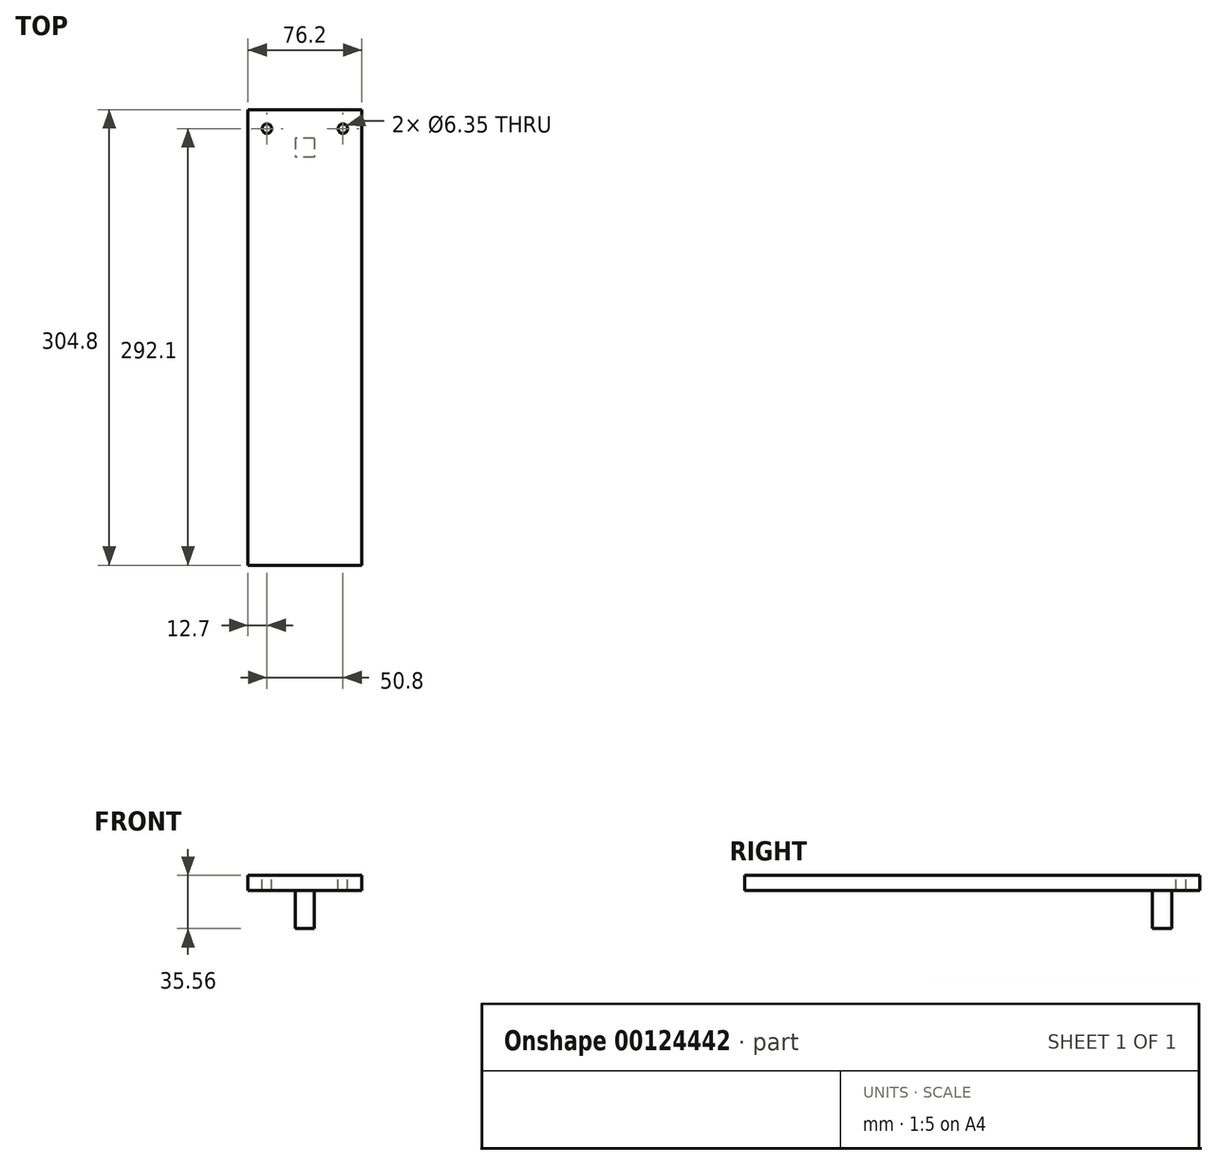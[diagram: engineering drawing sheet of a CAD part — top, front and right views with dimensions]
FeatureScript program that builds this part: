
annotation { "Feature Type Name" : "Feature", "Feature Type Description" : "" }
export const myFeature = defineFeature(function(context is Context, id is Id, definition is map)
    precondition{}
    {
        {
            var Q0;
            Q0=qCreatedBy(makeId("Top.planeOp"),FACE);
            var sketch = newSketch(context, id + "F0", { "sketchPlane" : qUnion([Q0])});
            skPoint(sketch, "E0.middle", {"position": v(0, 0) * mm});
            skLineSegment(sketch, "E1", {"start": v(-38.1, -76.2) * mm, "end": v(-38.1, 152.4) * mm});
            skLineSegment(sketch, "E2", {"start": v(38.1, -76.2) * mm, "end": v(38.1, 152.4) * mm});
            skLineSegment(sketch, "E3", {"start": v(38.1, 152.4) * mm, "end": v(-38.1, 152.4) * mm});
            skLineSegment(sketch, "E4", {"start": v(-38.1, -76.2) * mm, "end": v(-38.1, -152.4) * mm});
            skLineSegment(sketch, "E5", {"start": v(38.1, -76.2) * mm, "end": v(38.1, -152.4) * mm});
            skLineSegment(sketch, "E6", {"start": v(-38.1, -152.4) * mm, "end": v(38.1, -152.4) * mm});
            skSolve(sketch);
        }
        {
            var Q0;
            Q0=makeQuery(id+"F0.imprint","IMPRINT",FACE,{"disambiguationData":[TD([[makeQuery(id+"F0.imprint","IMPRINT",EDGE,{"derivedFrom":sQuery(id+"F0.wireOp",EDGE,"E1")}),-1.0]])]});
            extrude(context, id + "F1", {"entities" : qUnion([Q0]), "depth" : 10.16 * mm});
        }
        {
            var Q0;
            Q0=makeQuery(id+"F1.opExtrude","CAP_FACE",FACE,{"disambiguationData":[OSD([sQuery(id+"F0.wireOp",EDGE,"E1"),sQuery(id+"F0.wireOp",EDGE,"E2"),sQuery(id+"F0.wireOp",EDGE,"E3"),sQuery(id+"F0.wireOp",EDGE,"E4"),sQuery(id+"F0.wireOp",EDGE,"E5"),sQuery(id+"F0.wireOp",EDGE,"E6")])],"isStart":false});
            var sketch = newSketch(context, id + "F2", { "sketchPlane" : qUnion([Q0])});
            skCircle(sketch, "E7", {"center": v(25.4, 139.7) * mm, "radius": 3.18 * mm});
            skCircle(sketch, "E8", {"center": v(-25.4, 139.7) * mm, "radius": 3.18 * mm});
            skSolve(sketch);
        }
        {
            var Q0;
            Q0=makeQuery(id+"F2.imprint","IMPRINT",FACE,{"disambiguationData":[TD([[makeQuery(id+"F2.imprint","IMPRINT",EDGE,{"derivedFrom":sQuery(id+"F2.wireOp",EDGE,"E7")}),1.0]])]});
            var Q1;
            Q1=makeQuery(id+"F2.imprint","IMPRINT",FACE,{"disambiguationData":[TD([[makeQuery(id+"F2.imprint","IMPRINT",EDGE,{"derivedFrom":sQuery(id+"F2.wireOp",EDGE,"E8")}),1.0]])]});
            extrude(context, id + "F3", {"entities" : qUnion([Q0, Q1]), "operationType" : NewBodyOperationType.REMOVE, "oppositeDirection" : true, "depth" : 25.4 * mm});
        }
        {
            var Q0;
            Q0=makeQuery(id+"F1.opExtrude","CAP_FACE",FACE,{"disambiguationData":[OSD([sQuery(id+"F0.wireOp",EDGE,"E1"),sQuery(id+"F0.wireOp",EDGE,"E2"),sQuery(id+"F0.wireOp",EDGE,"E3"),sQuery(id+"F0.wireOp",EDGE,"E4"),sQuery(id+"F0.wireOp",EDGE,"E5"),sQuery(id+"F0.wireOp",EDGE,"E6")])],"isStart":true});
            var sketch = newSketch(context, id + "F4", { "sketchPlane" : qUnion([Q0])});
            skLineSegment(sketch, "E9", {"start": v(-38.1, -152.4) * mm, "end": v(-38.1, -127) * mm});
            skLineSegment(sketch, "E10.bottom", {"start": v(6.35, -133.35) * mm, "end": v(-6.35, -133.35) * mm});
            skLineSegment(sketch, "E10.top", {"start": v(6.35, -120.65) * mm, "end": v(-6.35, -120.65) * mm});
            skLineSegment(sketch, "E10.left", {"start": v(6.35, -133.35) * mm, "end": v(6.35, -120.65) * mm});
            skLineSegment(sketch, "E10.right", {"start": v(-6.35, -133.35) * mm, "end": v(-6.35, -120.65) * mm});
            skSolve(sketch);
        }
        {
            var Q0;
            Q0=makeQuery(id+"F4.imprint","IMPRINT",FACE,{"disambiguationData":[TD([[makeQuery(id+"F4.imprint","IMPRINT",EDGE,{"derivedFrom":sQuery(id+"F4.wireOp",EDGE,"E10.bottom")}),-1.0]])]});
            extrude(context, id + "F5", {"entities" : qUnion([Q0]), "operationType" : NewBodyOperationType.ADD, "depth" : 25.4 * mm});
        }
    });
